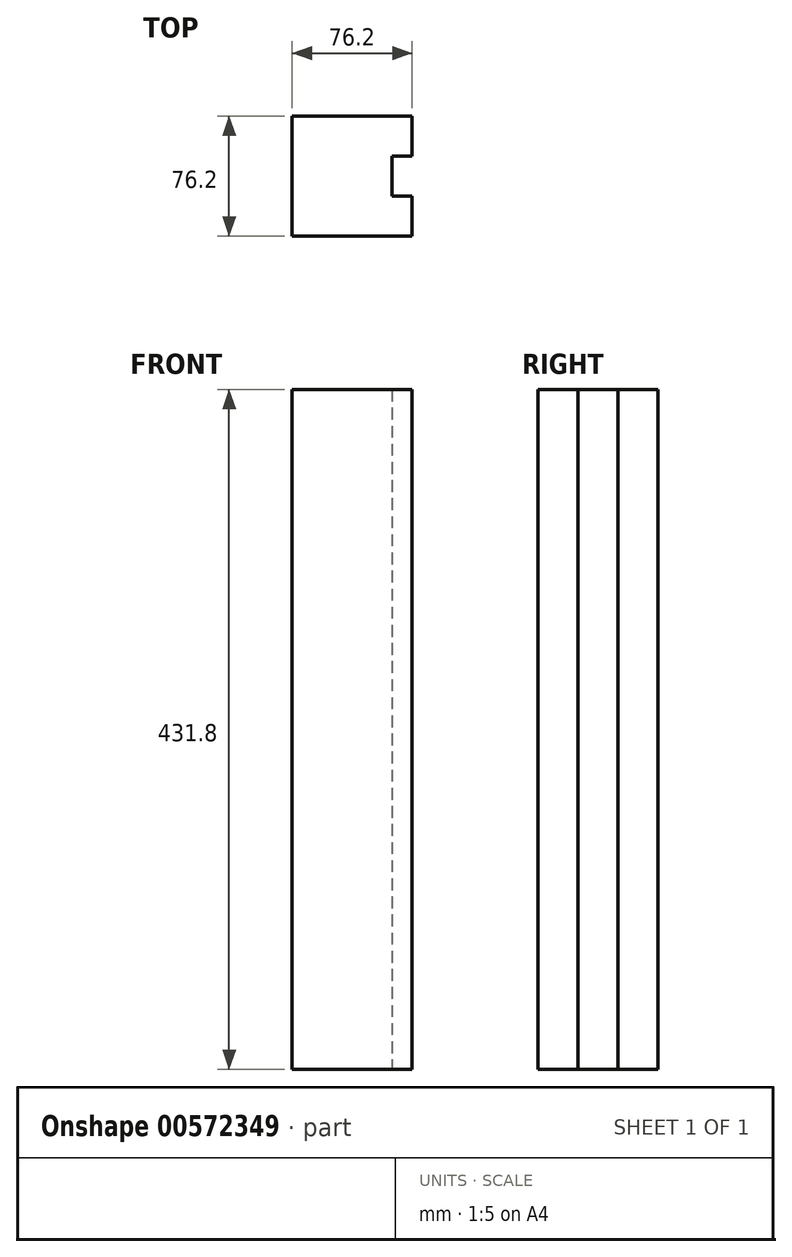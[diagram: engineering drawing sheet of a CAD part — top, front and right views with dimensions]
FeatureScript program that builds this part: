
annotation { "Feature Type Name" : "Feature", "Feature Type Description" : "" }
export const myFeature = defineFeature(function(context is Context, id is Id, definition is map)
    precondition{}
    {
        {
            var Q0;
            Q0=qCreatedBy(makeId("Top.planeOp"),FACE);
            var sketch = newSketch(context, id + "F0", { "sketchPlane" : qUnion([Q0])});
            skLineSegment(sketch, "E0.bottom", {"start": v(0, 0) * mm, "end": v(-76.2, 0) * mm});
            skLineSegment(sketch, "E0.top", {"start": v(0, 76.2) * mm, "end": v(-76.2, 76.2) * mm});
            skLineSegment(sketch, "E0.left", {"start": v(0, 0) * mm, "end": v(0, 25.4) * mm});
            skLineSegment(sketch, "E0.right", {"start": v(-76.2, 0) * mm, "end": v(-76.2, 76.2) * mm});
            skLineSegment(sketch, "E1.bottom", {"start": v(0, 50.8) * mm, "end": v(-12.7, 50.8) * mm});
            skLineSegment(sketch, "E1.top", {"start": v(0, 25.4) * mm, "end": v(-12.7, 25.4) * mm});
            skLineSegment(sketch, "E1.right", {"start": v(-12.7, 50.8) * mm, "end": v(-12.7, 25.4) * mm});
            skLineSegment(sketch, "E2.trimOffspring", {"start": v(0, 50.8) * mm, "end": v(0, 76.2) * mm});
            skSolve(sketch);
        }
        {
            var Q0;
            Q0=makeQuery(id+"F0.imprint","IMPRINT",FACE,{"disambiguationData":[TD([[makeQuery(id+"F0.imprint","IMPRINT",EDGE,{"derivedFrom":sQuery(id+"F0.wireOp",EDGE,"E0.bottom")}),-1.0]])]});
            extrude(context, id + "F1", {"entities" : qUnion([Q0]), "depth" : 431.8 * mm, "offsetDistance" : 25.4 * mm});
        }
    });
